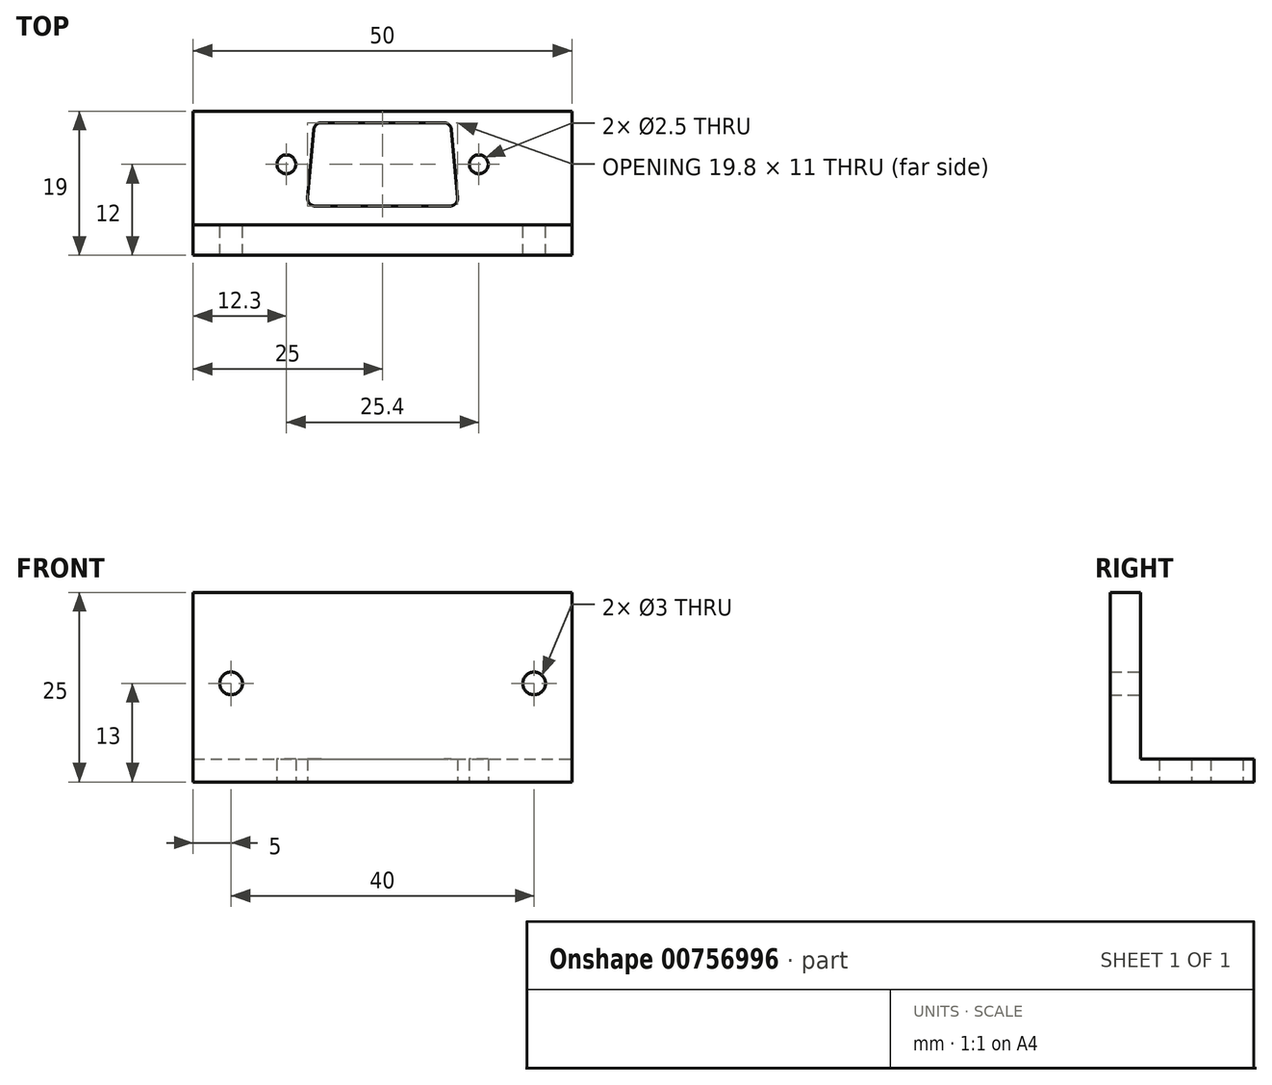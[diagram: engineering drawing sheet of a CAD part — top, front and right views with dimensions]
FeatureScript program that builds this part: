
annotation { "Feature Type Name" : "Feature", "Feature Type Description" : "" }
export const myFeature = defineFeature(function(context is Context, id is Id, definition is map)
    precondition{}
    {
        {
            var Q0;
            Q0=qCreatedBy(makeId("Top.planeOp"),FACE);
            var sketch = newSketch(context, id + "F0", { "sketchPlane" : qUnion([Q0])});
            skLineSegment(sketch, "E0.bottom", {"start": v(-25, 7) * mm, "end": v(25, 7) * mm});
            skLineSegment(sketch, "E0.top", {"start": v(-25, -8) * mm, "end": v(25, -8) * mm});
            skLineSegment(sketch, "E0.left", {"start": v(-25, 7) * mm, "end": v(-25, -8) * mm});
            skLineSegment(sketch, "E0.right", {"start": v(25, 7) * mm, "end": v(25, -8) * mm});
            skCircle(sketch, "E1", {"center": v(-12.7, 0) * mm, "radius": 1.25 * mm});
            skCircle(sketch, "E2", {"center": v(12.7, 0) * mm, "radius": 1.25 * mm});
            skLineSegment(sketch, "E3.top", {"start": v(-25, -12) * mm, "end": v(25, -12) * mm});
            skLineSegment(sketch, "E3.left", {"start": v(-25, -8) * mm, "end": v(-25, -12) * mm});
            skLineSegment(sketch, "E3.right", {"start": v(25, -8) * mm, "end": v(25, -12) * mm});
            skLineSegment(sketch, "E4.bottom", {"start": v(-8.09, 5.5) * mm, "end": v(8.09, 5.5) * mm});
            skLineSegment(sketch, "E4.top", {"start": v(-8.9, -5.5) * mm, "end": v(8.9, -5.5) * mm});
            skLineSegment(sketch, "E4.left", {"start": v(-9.08, 4.6) * mm, "end": v(-9.9, -4.4) * mm});
            skLineSegment(sketch, "E4.right", {"start": v(9.08, 4.6) * mm, "end": v(9.9, -4.4) * mm});
            skPoint(sketch, "E5.visualSharp", {"position": v(-10, -5.5) * mm});
            skArc(sketch, "E5.filletArc", {"start": v(-9.9, -4.4) * mm, "mid": v(-9.64, -5.17) * mm, "end": v(-8.9, -5.5) * mm});
            skPoint(sketch, "E6.visualSharp", {"position": v(10, -5.5) * mm});
            skArc(sketch, "E6.filletArc", {"start": v(8.9, -5.5) * mm, "mid": v(9.64, -5.17) * mm, "end": v(9.9, -4.4) * mm});
            skPoint(sketch, "E7.visualSharp", {"position": v(9, 5.5) * mm});
            skArc(sketch, "E7.filletArc", {"start": v(9.08, 4.6) * mm, "mid": v(8.76, 5.24) * mm, "end": v(8.09, 5.5) * mm});
            skPoint(sketch, "E8.visualSharp", {"position": v(-9, 5.5) * mm});
            skArc(sketch, "E8.filletArc", {"start": v(-8.09, 5.5) * mm, "mid": v(-8.76, 5.24) * mm, "end": v(-9.08, 4.6) * mm});
            skSolve(sketch);
        }
        {
            var Q0;
            Q0=makeQuery(id+"F0.imprint","IMPRINT",FACE,{"disambiguationData":[TD([[makeQuery(id+"F0.imprint","IMPRINT",EDGE,{"derivedFrom":sQuery(id+"F0.wireOp",EDGE,"E0.bottom")}),-1.0]])]});
            extrude(context, id + "F1", {"entities" : qUnion([Q0]), "depth" : 3 * mm, "offsetDistance" : 25 * mm});
        }
        {
            var Q0;
            Q0=makeQuery(id+"F0.imprint","IMPRINT",FACE,{"disambiguationData":[TD([[makeQuery(id+"F0.imprint","IMPRINT",EDGE,{"derivedFrom":sQuery(id+"F0.wireOp",EDGE,"E0.top")}),-1.0]])]});
            extrude(context, id + "F2", {"entities" : qUnion([Q0]), "operationType" : NewBodyOperationType.ADD, "depth" : 25 * mm, "offsetDistance" : 25 * mm});
        }
        {
            var Q0;
            Q0=makeQuery(id+"F2.opExtrude","SWEPT_FACE",FACE,{"disambiguationData":[OSD([sQuery(id+"F0.wireOp",EDGE,"E0.top")])]});
            cPlane(context, id + "F3", {"entities" : qUnion([Q0]), "cplaneType" : CPlaneType.OFFSET, "offset" : 0 * mm, "width" : 150 * mm, "height" : 150 * mm});
        }
        {
            var Q0;
            Q0=qCreatedBy(id+"F3.planeOp",FACE);
            var sketch = newSketch(context, id + "F4", { "sketchPlane" : qUnion([Q0])});
            skLineSegment(sketch, "E9", {"start": v(-36.64, 13) * mm, "end": v(36.38, 13) * mm, "construction": true});
            skLineSegment(sketch, "E10", {"start": v(20, 36.78) * mm, "end": v(20, 0) * mm, "construction": true});
            skLineSegment(sketch, "E11", {"start": v(-20, 36.78) * mm, "end": v(-20, 0) * mm, "construction": true});
            skCircle(sketch, "E12", {"center": v(-20, 13) * mm, "radius": 1.5 * mm});
            skCircle(sketch, "E13", {"center": v(20, 13) * mm, "radius": 1.5 * mm});
            skSolve(sketch);
        }
        {
            var Q0;
            Q0=makeQuery(id+"F4.imprint","IMPRINT",FACE,{"disambiguationData":[TD([[makeQuery(id+"F4.imprint","IMPRINT",EDGE,{"derivedFrom":sQuery(id+"F4.wireOp",EDGE,"E12")}),1.0]])]});
            var Q1;
            Q1=makeQuery(id+"F4.imprint","IMPRINT",FACE,{"disambiguationData":[TD([[makeQuery(id+"F4.imprint","IMPRINT",EDGE,{"derivedFrom":sQuery(id+"F4.wireOp",EDGE,"E13")}),1.0]])]});
            extrude(context, id + "F5", {"entities" : qUnion([Q0, Q1]), "operationType" : NewBodyOperationType.REMOVE, "endBound" : BoundingType.THROUGH_ALL, "oppositeDirection" : true, "depth" : 25 * mm, "offsetDistance" : 25 * mm});
        }
    });
